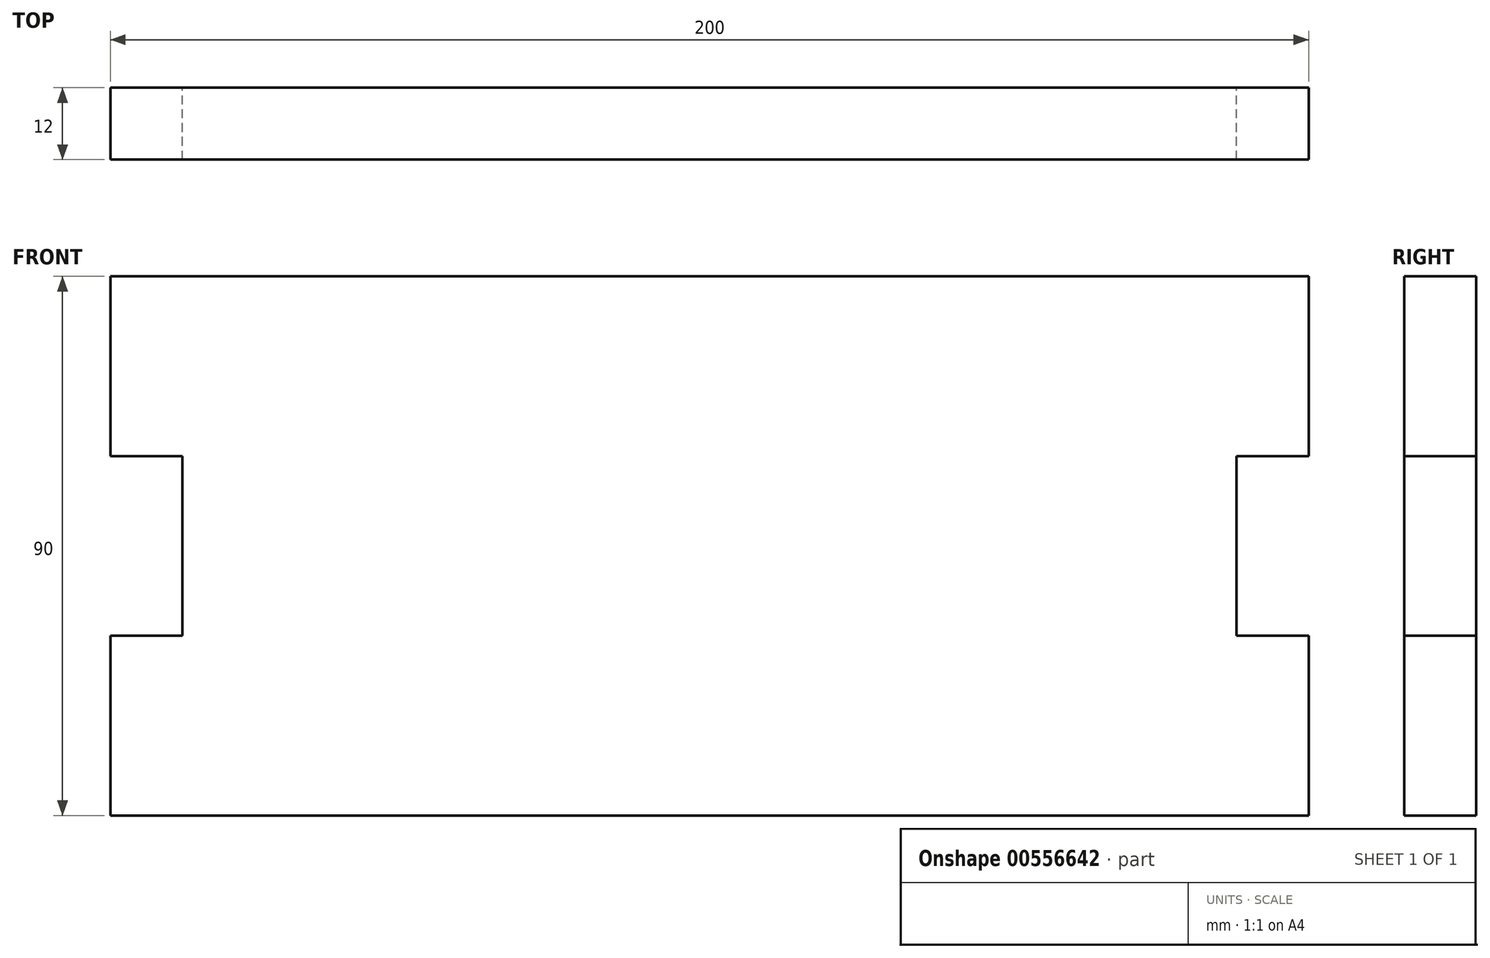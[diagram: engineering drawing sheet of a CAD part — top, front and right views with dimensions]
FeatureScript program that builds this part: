
annotation { "Feature Type Name" : "Feature", "Feature Type Description" : "" }
export const myFeature = defineFeature(function(context is Context, id is Id, definition is map)
    precondition{}
    {
        {
            var Q0;
            Q0=qCreatedBy(makeId("Front.planeOp"),FACE);
            var sketch = newSketch(context, id + "F0", { "sketchPlane" : qUnion([Q0])});
            skLineSegment(sketch, "E0", {"start": v(0, 0) * mm, "end": v(0, 30) * mm});
            skLineSegment(sketch, "E1", {"start": v(0, 30) * mm, "end": v(12, 30) * mm});
            skLineSegment(sketch, "E2", {"start": v(12, 30) * mm, "end": v(12, 60) * mm});
            skLineSegment(sketch, "E3", {"start": v(12, 60) * mm, "end": v(0, 60) * mm});
            skLineSegment(sketch, "E4", {"start": v(0, 60) * mm, "end": v(0, 90) * mm});
            skLineSegment(sketch, "E5", {"start": v(0, 90) * mm, "end": v(100, 90) * mm});
            skLineSegment(sketch, "E6", {"start": v(100, 90) * mm, "end": v(100, 0) * mm, "construction": true});
            skLineSegment(sketch, "E7", {"start": v(100, 0) * mm, "end": v(0, 0) * mm});
            skLineSegment(sketch, "E8.MirrorCS", {"start": v(200, 30) * mm, "end": v(188, 30) * mm});
            skLineSegment(sketch, "E9.MirrorCS", {"start": v(188, 30) * mm, "end": v(188, 60) * mm});
            skLineSegment(sketch, "E10.MirrorCS", {"start": v(200, 60) * mm, "end": v(200, 90) * mm});
            skLineSegment(sketch, "E11.MirrorCS", {"start": v(100, 0) * mm, "end": v(200, 0) * mm});
            skLineSegment(sketch, "E12.MirrorCS", {"start": v(188, 60) * mm, "end": v(200, 60) * mm});
            skLineSegment(sketch, "E13.MirrorCS", {"start": v(200, 0) * mm, "end": v(200, 30) * mm});
            skLineSegment(sketch, "E14.MirrorCS", {"start": v(200, 90) * mm, "end": v(100, 90) * mm});
            skSolve(sketch);
        }
        {
            var Q0;
            Q0 = qSketchRegion(id + "F0", true);
            extrude(context, id + "F1", {"entities" : qUnion([Q0]), "endBound" : BoundingType.SYMMETRIC, "depth" : 12 * mm, "offsetDistance" : 25 * mm});
        }
    });
